# Revit family: A4S
name_source: partatom
category: Lighting Fixtures
revit_build: Autodesk Revit 2014 (Build: 20130308_1515(x64)
units: mm (PartAtom-declared; Revit-internal decimal feet)

## types (1)
- A4S
    Certifications = CSA,Chicago Plenum,Non-IC,UL
    Color Filter = 16777215
    Depth = 0' - 4 13/16"
    Description = 4" ADJUSTABLE DOWNLIGHTS
    Dimming Lamp Color Temperature Shift = <None>
    Features = 45º vertical and 362º horizontal aiming
45º vertical aiming with visual aiming markers
All trims feature center beam optics
Electronic transformer standard (low voltage models)
Hot aiming standard for all trims
Horizontal and vertical adjustment can be locked in position
B24 bar hangers sold separately for T-bar ceilings
    Lamp = 50W MR16
    Length = 0' - 11 11/16"
    Manufacturer = PRESCOLITE
    Model = A4S
    Photometric Web File = a4smr-4b1whwt_30_degree_lamp_50mr16q_25_nfl_t_fpc.ies
    Photometric Web Link = https://www.hubbell.com
    Product Documentation Link = https://hubbellcdn.com
    Product Page URL = https://www.hubbell.com
    Reflector = <By Category>
    Tilt Angle = 60.00°
    Trim = White
    URL = https://www.hubbell.com
    Warranty = 5 Year Warranty
    Wattage Comments = 50W
    Width = 1' - 2 3/8"

## geometry (parser evidence)
native form markers: Sweep x1
no freeform markers — native parametric forms only
